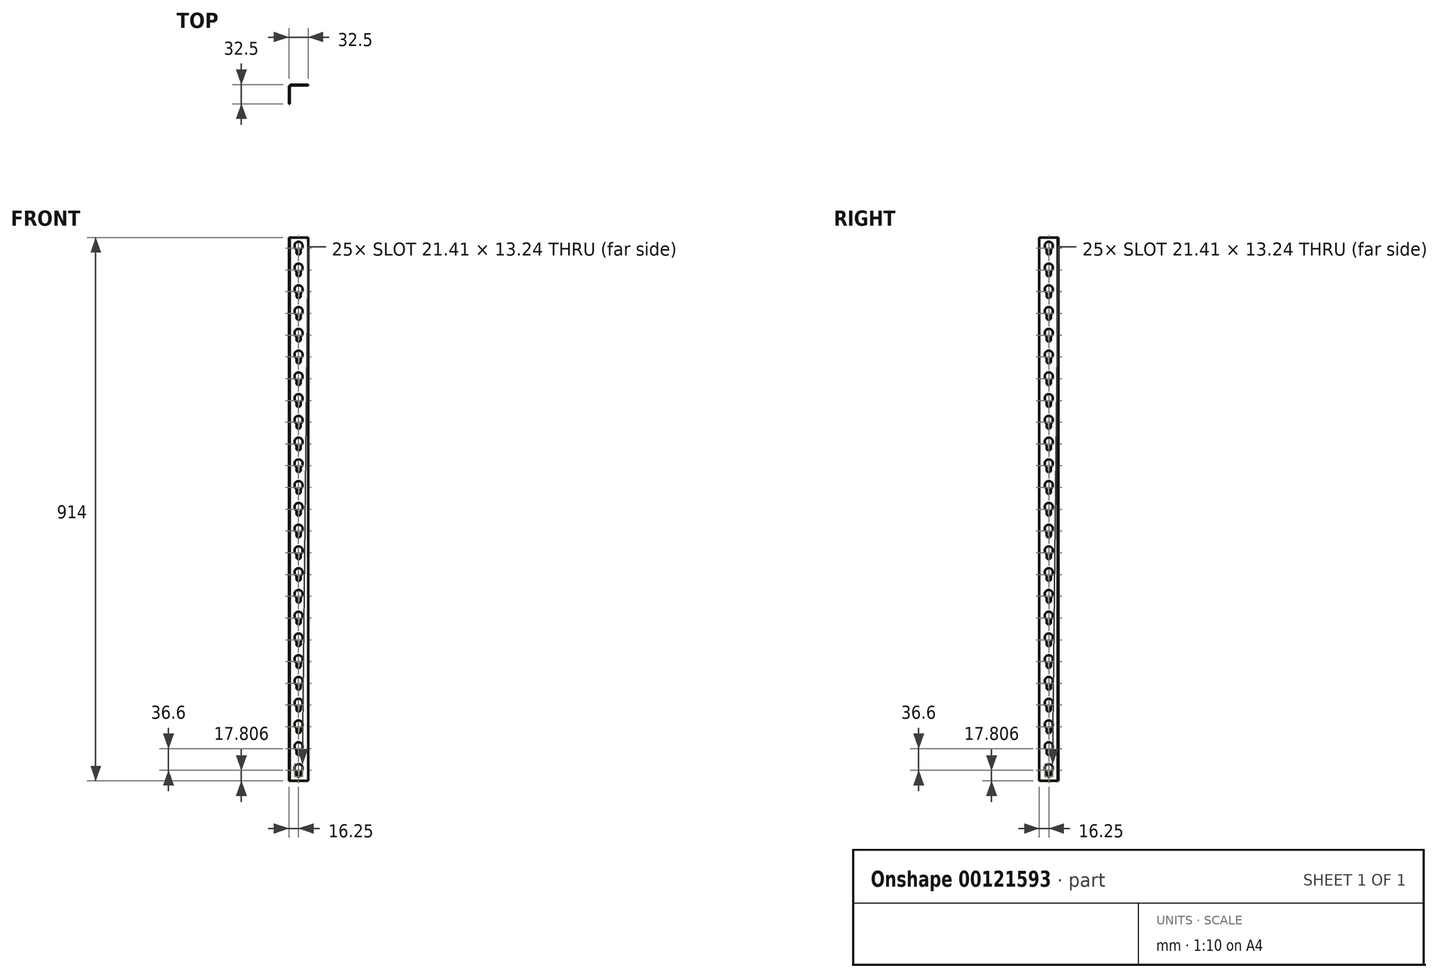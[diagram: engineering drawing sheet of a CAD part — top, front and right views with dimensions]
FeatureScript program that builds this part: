
annotation { "Feature Type Name" : "Feature", "Feature Type Description" : "" }
export const myFeature = defineFeature(function(context is Context, id is Id, definition is map)
    precondition{}
    {
        {
            var Q0;
            Q0=qCreatedBy(makeId("Top.planeOp"),FACE);
            var sketch = newSketch(context, id + "F0", { "sketchPlane" : qUnion([Q0])});
            skLineSegment(sketch, "E0", {"start": v(-1.5, 0) * mm, "end": v(-1.5, 1.5) * mm});
            skLineSegment(sketch, "E1", {"start": v(-1.5, 1.5) * mm, "end": v(31, 1.5) * mm});
            skLineSegment(sketch, "E2.0", {"start": v(0, 0) * mm, "end": v(31, 0) * mm});
            skLineSegment(sketch, "E2.1", {"start": v(0, 0) * mm, "end": v(0, 0) * mm});
            skLineSegment(sketch, "E3", {"start": v(31, 1.5) * mm, "end": v(31, 0) * mm});
            skLineSegment(sketch, "E4", {"start": v(0, 0) * mm, "end": v(-1.5, 0) * mm});
            skSolve(sketch);
        }
        {
            var Q0;
            Q0 = qSketchRegion(id + "F0", true);
            extrude(context, id + "F1", {"entities" : qUnion([Q0]), "depth" : 914 * mm});
        }
        {
            var Q0;
            Q0=makeQuery(id+"F1.opExtrude","SWEPT_FACE",FACE,{"disambiguationData":[OSD([sQuery(id+"F0.wireOp",EDGE,"E2.0")])]});
            var sketch = newSketch(context, id + "F2", { "sketchPlane" : qUnion([Q0])});
            skPoint(sketch, "E5.centerSnap0", {"position": v(14.75, 0) * mm});
            skLineSegment(sketch, "E6", {"start": v(18.45, 10.8) * mm, "end": v(18.45, 15.8) * mm});
            skLineSegment(sketch, "E7", {"start": v(11.05, 10.8) * mm, "end": v(11.05, 15.8) * mm});
            skArc(sketch, "E8", {"start": v(11.05, 10.8) * mm, "mid": v(14.75, 7.1) * mm, "end": v(18.45, 10.8) * mm});
            skArc(sketch, "E9", {"start": v(18.45, 15.8) * mm, "mid": v(14.75, 28.51) * mm, "end": v(11.05, 15.8) * mm});
            skLineSegment(sketch, "E10.0.1.0", {"start": v(11.05, 47.4) * mm, "end": v(11.05, 52.4) * mm});
            skLineSegment(sketch, "E10.0.1.1", {"start": v(18.45, 47.4) * mm, "end": v(18.45, 52.4) * mm});
            skArc(sketch, "E10.0.1.2", {"start": v(11.05, 47.4) * mm, "mid": v(14.75, 43.7) * mm, "end": v(18.45, 47.4) * mm});
            skArc(sketch, "E10.0.1.3", {"start": v(18.45, 52.4) * mm, "mid": v(14.75, 65.11) * mm, "end": v(11.05, 52.4) * mm});
            skLineSegment(sketch, "E10.0.2.0", {"start": v(11.05, 84) * mm, "end": v(11.05, 89) * mm});
            skLineSegment(sketch, "E10.0.2.1", {"start": v(18.45, 84) * mm, "end": v(18.45, 89) * mm});
            skArc(sketch, "E10.0.2.2", {"start": v(11.05, 84) * mm, "mid": v(14.75, 80.3) * mm, "end": v(18.45, 84) * mm});
            skArc(sketch, "E10.0.2.3", {"start": v(18.45, 89) * mm, "mid": v(14.75, 101.71) * mm, "end": v(11.05, 89) * mm});
            skLineSegment(sketch, "E10.0.3.0", {"start": v(11.05, 120.6) * mm, "end": v(11.05, 125.6) * mm});
            skLineSegment(sketch, "E10.0.3.1", {"start": v(18.45, 120.6) * mm, "end": v(18.45, 125.6) * mm});
            skArc(sketch, "E10.0.3.2", {"start": v(11.05, 120.6) * mm, "mid": v(14.75, 116.9) * mm, "end": v(18.45, 120.6) * mm});
            skArc(sketch, "E10.0.3.3", {"start": v(18.45, 125.6) * mm, "mid": v(14.75, 138.31) * mm, "end": v(11.05, 125.6) * mm});
            skLineSegment(sketch, "E10.0.4.0", {"start": v(11.05, 157.2) * mm, "end": v(11.05, 162.2) * mm});
            skLineSegment(sketch, "E10.0.4.1", {"start": v(18.45, 157.2) * mm, "end": v(18.45, 162.2) * mm});
            skArc(sketch, "E10.0.4.2", {"start": v(11.05, 157.2) * mm, "mid": v(14.75, 153.5) * mm, "end": v(18.45, 157.2) * mm});
            skArc(sketch, "E10.0.4.3", {"start": v(18.45, 162.2) * mm, "mid": v(14.75, 174.91) * mm, "end": v(11.05, 162.2) * mm});
            skLineSegment(sketch, "E10.0.5.0", {"start": v(11.05, 193.8) * mm, "end": v(11.05, 198.8) * mm});
            skLineSegment(sketch, "E10.0.5.1", {"start": v(18.45, 193.8) * mm, "end": v(18.45, 198.8) * mm});
            skArc(sketch, "E10.0.5.2", {"start": v(11.05, 193.8) * mm, "mid": v(14.75, 190.1) * mm, "end": v(18.45, 193.8) * mm});
            skArc(sketch, "E10.0.5.3", {"start": v(18.45, 198.8) * mm, "mid": v(14.75, 211.51) * mm, "end": v(11.05, 198.8) * mm});
            skLineSegment(sketch, "E10.direction1", {"start": v(11.05, 10.8) * mm, "end": v(36.05, 10.8) * mm, "construction": true});
            skLineSegment(sketch, "E10.direction2", {"start": v(11.05, 10.8) * mm, "end": v(11.05, 47.4) * mm, "construction": true});
            skLineSegment(sketch, "E11.0.0.6", {"start": v(11.05, 230.4) * mm, "end": v(11.05, 235.4) * mm});
            skLineSegment(sketch, "E11.3.0.6", {"start": v(18.45, 230.4) * mm, "end": v(18.45, 235.4) * mm});
            skArc(sketch, "E11.6.0.6", {"start": v(11.05, 230.4) * mm, "mid": v(14.75, 226.7) * mm, "end": v(18.45, 230.4) * mm});
            skArc(sketch, "E11.10.0.6", {"start": v(18.45, 235.4) * mm, "mid": v(14.75, 248.11) * mm, "end": v(11.05, 235.4) * mm});
            skLineSegment(sketch, "E12.0.0.7", {"start": v(11.05, 267) * mm, "end": v(11.05, 272) * mm});
            skLineSegment(sketch, "E12.3.0.7", {"start": v(18.45, 267) * mm, "end": v(18.45, 272) * mm});
            skArc(sketch, "E12.6.0.7", {"start": v(11.05, 267) * mm, "mid": v(14.75, 263.3) * mm, "end": v(18.45, 267) * mm});
            skArc(sketch, "E12.10.0.7", {"start": v(18.45, 272) * mm, "mid": v(14.75, 284.71) * mm, "end": v(11.05, 272) * mm});
            skLineSegment(sketch, "E12.0.0.8", {"start": v(11.05, 303.6) * mm, "end": v(11.05, 308.6) * mm});
            skLineSegment(sketch, "E12.3.0.8", {"start": v(18.45, 303.6) * mm, "end": v(18.45, 308.6) * mm});
            skArc(sketch, "E12.6.0.8", {"start": v(11.05, 303.6) * mm, "mid": v(14.75, 299.9) * mm, "end": v(18.45, 303.6) * mm});
            skArc(sketch, "E12.10.0.8", {"start": v(18.45, 308.6) * mm, "mid": v(14.75, 321.31) * mm, "end": v(11.05, 308.6) * mm});
            skLineSegment(sketch, "E12.0.0.9", {"start": v(11.05, 340.2) * mm, "end": v(11.05, 345.2) * mm});
            skLineSegment(sketch, "E12.3.0.9", {"start": v(18.45, 340.2) * mm, "end": v(18.45, 345.2) * mm});
            skArc(sketch, "E12.6.0.9", {"start": v(11.05, 340.2) * mm, "mid": v(14.75, 336.5) * mm, "end": v(18.45, 340.2) * mm});
            skArc(sketch, "E12.10.0.9", {"start": v(18.45, 345.2) * mm, "mid": v(14.75, 357.91) * mm, "end": v(11.05, 345.2) * mm});
            skLineSegment(sketch, "E12.0.0.10", {"start": v(11.05, 376.8) * mm, "end": v(11.05, 381.8) * mm});
            skLineSegment(sketch, "E12.3.0.10", {"start": v(18.45, 376.8) * mm, "end": v(18.45, 381.8) * mm});
            skArc(sketch, "E12.6.0.10", {"start": v(11.05, 376.8) * mm, "mid": v(14.75, 373.1) * mm, "end": v(18.45, 376.8) * mm});
            skArc(sketch, "E12.10.0.10", {"start": v(18.45, 381.8) * mm, "mid": v(14.75, 394.51) * mm, "end": v(11.05, 381.8) * mm});
            skLineSegment(sketch, "E12.0.0.11", {"start": v(11.05, 413.4) * mm, "end": v(11.05, 418.4) * mm});
            skLineSegment(sketch, "E12.3.0.11", {"start": v(18.45, 413.4) * mm, "end": v(18.45, 418.4) * mm});
            skArc(sketch, "E12.6.0.11", {"start": v(11.05, 413.4) * mm, "mid": v(14.75, 409.7) * mm, "end": v(18.45, 413.4) * mm});
            skArc(sketch, "E12.10.0.11", {"start": v(18.45, 418.4) * mm, "mid": v(14.75, 431.11) * mm, "end": v(11.05, 418.4) * mm});
            skLineSegment(sketch, "E12.0.0.12", {"start": v(11.05, 450) * mm, "end": v(11.05, 455) * mm});
            skLineSegment(sketch, "E12.3.0.12", {"start": v(18.45, 450) * mm, "end": v(18.45, 455) * mm});
            skArc(sketch, "E12.6.0.12", {"start": v(11.05, 450) * mm, "mid": v(14.75, 446.3) * mm, "end": v(18.45, 450) * mm});
            skArc(sketch, "E12.10.0.12", {"start": v(18.45, 455) * mm, "mid": v(14.75, 467.71) * mm, "end": v(11.05, 455) * mm});
            skLineSegment(sketch, "E12.0.0.13", {"start": v(11.05, 486.6) * mm, "end": v(11.05, 491.6) * mm});
            skLineSegment(sketch, "E12.3.0.13", {"start": v(18.45, 486.6) * mm, "end": v(18.45, 491.6) * mm});
            skArc(sketch, "E12.6.0.13", {"start": v(11.05, 486.6) * mm, "mid": v(14.75, 482.9) * mm, "end": v(18.45, 486.6) * mm});
            skArc(sketch, "E12.10.0.13", {"start": v(18.45, 491.6) * mm, "mid": v(14.75, 504.31) * mm, "end": v(11.05, 491.6) * mm});
            skLineSegment(sketch, "E12.0.0.14", {"start": v(11.05, 523.2) * mm, "end": v(11.05, 528.2) * mm});
            skLineSegment(sketch, "E12.3.0.14", {"start": v(18.45, 523.2) * mm, "end": v(18.45, 528.2) * mm});
            skArc(sketch, "E12.6.0.14", {"start": v(11.05, 523.2) * mm, "mid": v(14.75, 519.5) * mm, "end": v(18.45, 523.2) * mm});
            skArc(sketch, "E12.10.0.14", {"start": v(18.45, 528.2) * mm, "mid": v(14.75, 540.91) * mm, "end": v(11.05, 528.2) * mm});
            skLineSegment(sketch, "E12.0.0.15", {"start": v(11.05, 559.8) * mm, "end": v(11.05, 564.8) * mm});
            skLineSegment(sketch, "E12.3.0.15", {"start": v(18.45, 559.8) * mm, "end": v(18.45, 564.8) * mm});
            skArc(sketch, "E12.6.0.15", {"start": v(11.05, 559.8) * mm, "mid": v(14.75, 556.1) * mm, "end": v(18.45, 559.8) * mm});
            skArc(sketch, "E12.10.0.15", {"start": v(18.45, 564.8) * mm, "mid": v(14.75, 577.51) * mm, "end": v(11.05, 564.8) * mm});
            skLineSegment(sketch, "E12.0.0.16", {"start": v(11.05, 596.4) * mm, "end": v(11.05, 601.4) * mm});
            skLineSegment(sketch, "E12.3.0.16", {"start": v(18.45, 596.4) * mm, "end": v(18.45, 601.4) * mm});
            skArc(sketch, "E12.6.0.16", {"start": v(11.05, 596.4) * mm, "mid": v(14.75, 592.7) * mm, "end": v(18.45, 596.4) * mm});
            skArc(sketch, "E12.10.0.16", {"start": v(18.45, 601.4) * mm, "mid": v(14.75, 614.11) * mm, "end": v(11.05, 601.4) * mm});
            skLineSegment(sketch, "E12.0.0.17", {"start": v(11.05, 633) * mm, "end": v(11.05, 638) * mm});
            skLineSegment(sketch, "E12.3.0.17", {"start": v(18.45, 633) * mm, "end": v(18.45, 638) * mm});
            skArc(sketch, "E12.6.0.17", {"start": v(11.05, 633) * mm, "mid": v(14.75, 629.3) * mm, "end": v(18.45, 633) * mm});
            skArc(sketch, "E12.10.0.17", {"start": v(18.45, 638) * mm, "mid": v(14.75, 650.71) * mm, "end": v(11.05, 638) * mm});
            skLineSegment(sketch, "E12.0.0.18", {"start": v(11.05, 669.6) * mm, "end": v(11.05, 674.6) * mm});
            skLineSegment(sketch, "E12.3.0.18", {"start": v(18.45, 669.6) * mm, "end": v(18.45, 674.6) * mm});
            skArc(sketch, "E12.6.0.18", {"start": v(11.05, 669.6) * mm, "mid": v(14.75, 665.9) * mm, "end": v(18.45, 669.6) * mm});
            skArc(sketch, "E12.10.0.18", {"start": v(18.45, 674.6) * mm, "mid": v(14.75, 687.31) * mm, "end": v(11.05, 674.6) * mm});
            skLineSegment(sketch, "E12.0.0.19", {"start": v(11.05, 706.2) * mm, "end": v(11.05, 711.2) * mm});
            skLineSegment(sketch, "E12.3.0.19", {"start": v(18.45, 706.2) * mm, "end": v(18.45, 711.2) * mm});
            skArc(sketch, "E12.6.0.19", {"start": v(11.05, 706.2) * mm, "mid": v(14.75, 702.5) * mm, "end": v(18.45, 706.2) * mm});
            skArc(sketch, "E12.10.0.19", {"start": v(18.45, 711.2) * mm, "mid": v(14.75, 723.91) * mm, "end": v(11.05, 711.2) * mm});
            skLineSegment(sketch, "E12.0.0.20", {"start": v(11.05, 742.8) * mm, "end": v(11.05, 747.8) * mm});
            skLineSegment(sketch, "E12.3.0.20", {"start": v(18.45, 742.8) * mm, "end": v(18.45, 747.8) * mm});
            skArc(sketch, "E12.6.0.20", {"start": v(11.05, 742.8) * mm, "mid": v(14.75, 739.1) * mm, "end": v(18.45, 742.8) * mm});
            skArc(sketch, "E12.10.0.20", {"start": v(18.45, 747.8) * mm, "mid": v(14.75, 760.51) * mm, "end": v(11.05, 747.8) * mm});
            skLineSegment(sketch, "E12.0.0.21", {"start": v(11.05, 779.4) * mm, "end": v(11.05, 784.4) * mm});
            skLineSegment(sketch, "E12.3.0.21", {"start": v(18.45, 779.4) * mm, "end": v(18.45, 784.4) * mm});
            skArc(sketch, "E12.6.0.21", {"start": v(11.05, 779.4) * mm, "mid": v(14.75, 775.7) * mm, "end": v(18.45, 779.4) * mm});
            skArc(sketch, "E12.10.0.21", {"start": v(18.45, 784.4) * mm, "mid": v(14.75, 797.11) * mm, "end": v(11.05, 784.4) * mm});
            skLineSegment(sketch, "E13.0.0.22", {"start": v(11.05, 816) * mm, "end": v(11.05, 821) * mm});
            skLineSegment(sketch, "E13.3.0.22", {"start": v(18.45, 816) * mm, "end": v(18.45, 821) * mm});
            skArc(sketch, "E13.6.0.22", {"start": v(11.05, 816) * mm, "mid": v(14.75, 812.3) * mm, "end": v(18.45, 816) * mm});
            skArc(sketch, "E13.10.0.22", {"start": v(18.45, 821) * mm, "mid": v(14.75, 833.71) * mm, "end": v(11.05, 821) * mm});
            skLineSegment(sketch, "E13.0.0.23", {"start": v(11.05, 852.6) * mm, "end": v(11.05, 857.6) * mm});
            skLineSegment(sketch, "E13.3.0.23", {"start": v(18.45, 852.6) * mm, "end": v(18.45, 857.6) * mm});
            skArc(sketch, "E13.6.0.23", {"start": v(11.05, 852.6) * mm, "mid": v(14.75, 848.9) * mm, "end": v(18.45, 852.6) * mm});
            skArc(sketch, "E13.10.0.23", {"start": v(18.45, 857.6) * mm, "mid": v(14.75, 870.31) * mm, "end": v(11.05, 857.6) * mm});
            skLineSegment(sketch, "E14.0.0.24", {"start": v(11.05, 889.2) * mm, "end": v(11.05, 894.2) * mm});
            skLineSegment(sketch, "E14.3.0.24", {"start": v(18.45, 889.2) * mm, "end": v(18.45, 894.2) * mm});
            skArc(sketch, "E14.6.0.24", {"start": v(11.05, 889.2) * mm, "mid": v(14.75, 885.5) * mm, "end": v(18.45, 889.2) * mm});
            skArc(sketch, "E14.10.0.24", {"start": v(18.45, 894.2) * mm, "mid": v(14.75, 906.91) * mm, "end": v(11.05, 894.2) * mm});
            skLineSegment(sketch, "E15", {"start": v(0, 0) * mm, "end": v(0, 914) * mm, "construction": true});
            skSolve(sketch);
        }
        {
            var Q0;
            Q0 = qSketchRegion(id + "F2", true);
            extrude(context, id + "F3", {"entities" : qUnion([Q0]), "operationType" : NewBodyOperationType.REMOVE, "endBound" : BoundingType.UP_TO_NEXT, "oppositeDirection" : true, "depth" : 25 * mm});
        }
        {
            var Q0;
            Q0=makeQuery(id+"F1.opExtrude","SWEPT_BODY",BODY,{"disambiguationData":[OSD([sQuery(id+"F0.wireOp",EDGE,"E0"),sQuery(id+"F0.wireOp",EDGE,"E1"),sQuery(id+"F0.wireOp",EDGE,"E2.0"),sQuery(id+"F0.wireOp",EDGE,"E3"),sQuery(id+"F0.wireOp",EDGE,"E4")])]});
            var Q1;
            Q1=makeQuery(id+"F1.opExtrude","SWEPT_EDGE",EDGE,{"disambiguationData":[OSD([sQuery(id+"F0.wireOp",EDGE,"E0"),sQuery(id+"F0.wireOp",EDGE,"E4")])]});
            transform(context, id + "F4", {"entities" : qUnion([Q0]), "transformType" : TransformType.ROTATION, "transformAxis" : qUnion([Q1]), "angle" : 90 * degree, "makeCopy" : true});
        }
        {
            var Q0;
            Q0=makeQuery(id+"F4.opPattern","COPY",BODY,{"derivedFrom":makeQuery(id+"F1.opExtrude","SWEPT_BODY",BODY,{"disambiguationData":[OSD([sQuery(id+"F0.wireOp",EDGE,"E0"),sQuery(id+"F0.wireOp",EDGE,"E1"),sQuery(id+"F0.wireOp",EDGE,"E2.0"),sQuery(id+"F0.wireOp",EDGE,"E3"),sQuery(id+"F0.wireOp",EDGE,"E4")])]}),"instanceName":"1"});
            var Q1;
            Q1=makeQuery(id+"F1.opExtrude","CAP_VERTEX",VERTEX,{"disambiguationData":[OSD([sQuery(id+"F0.wireOp",EDGE,"E0"),sQuery(id+"F0.wireOp",EDGE,"E4")])],"isStart":true});
            var Q2;
            Q2=makeQuery(id+"F1.opExtrude","CAP_VERTEX",VERTEX,{"disambiguationData":[OSD([sQuery(id+"F0.wireOp",EDGE,"E0"),sQuery(id+"F0.wireOp",EDGE,"E1")])],"isStart":true});
            transform(context, id + "F5", {"entities" : qUnion([Q0]), "transformType" : TransformType.TRANSLATION_ENTITY, "oppositeDirectionEntity" : false, "transformLine" : qUnion([Q1, Q2]), "makeCopy" : false});
        }
        {
            var Q0;
            Q0=makeQuery(id+"F4.opPattern","COPY",BODY,{"derivedFrom":makeQuery(id+"F1.opExtrude","SWEPT_BODY",BODY,{"disambiguationData":[OSD([sQuery(id+"F0.wireOp",EDGE,"E0"),sQuery(id+"F0.wireOp",EDGE,"E1"),sQuery(id+"F0.wireOp",EDGE,"E2.0"),sQuery(id+"F0.wireOp",EDGE,"E3"),sQuery(id+"F0.wireOp",EDGE,"E4")])]}),"instanceName":"1"});
            var Q1;
            Q1=makeQuery(id+"F1.opExtrude","SWEPT_BODY",BODY,{"disambiguationData":[OSD([sQuery(id+"F0.wireOp",EDGE,"E0"),sQuery(id+"F0.wireOp",EDGE,"E1"),sQuery(id+"F0.wireOp",EDGE,"E2.0"),sQuery(id+"F0.wireOp",EDGE,"E3"),sQuery(id+"F0.wireOp",EDGE,"E4")])]});
            booleanBodies(context, id + "F6", {"operationType" : BooleanOperationType.UNION, "tools" : qUnion([Q0, Q1])});
        }
        {
            var Q0;
            Q0=makeQuery(id+"F6.opBoolean","INTERSECT",EDGE,{"derivedFrom":[makeQuery(id+"F1.opExtrude","SWEPT_FACE",FACE,{"disambiguationData":[OSD([sQuery(id+"F0.wireOp",EDGE,"E2.0"),sQuery(id+"F0.wireOp",EDGE,"E4")])]}),makeQuery(id+"F4.opPattern","COPY",FACE,{"derivedFrom":makeQuery(id+"F1.opExtrude","SWEPT_FACE",FACE,{"disambiguationData":[OSD([sQuery(id+"F0.wireOp",EDGE,"E1")])]}),"instanceName":"1"})]});
            fillet(context, id + "F7", {"entities" : qUnion([Q0]), "radius" : 4 * mm, "tangentPropagation" : true, "allowEdgeOverflow" : false});
        }
        {
            var Q0;
            Q0=makeQuery(id+"F4.opPattern","COPY",EDGE,{"derivedFrom":makeQuery(id+"F1.opExtrude","SWEPT_EDGE",EDGE,{"disambiguationData":[OSD([sQuery(id+"F0.wireOp",EDGE,"E0"),sQuery(id+"F0.wireOp",EDGE,"E4")])]}),"instanceName":"1"});
            fillet(context, id + "F8", {"entities" : qUnion([Q0]), "radius" : 5 * mm, "tangentPropagation" : true, "allowEdgeOverflow" : false});
        }
    });
